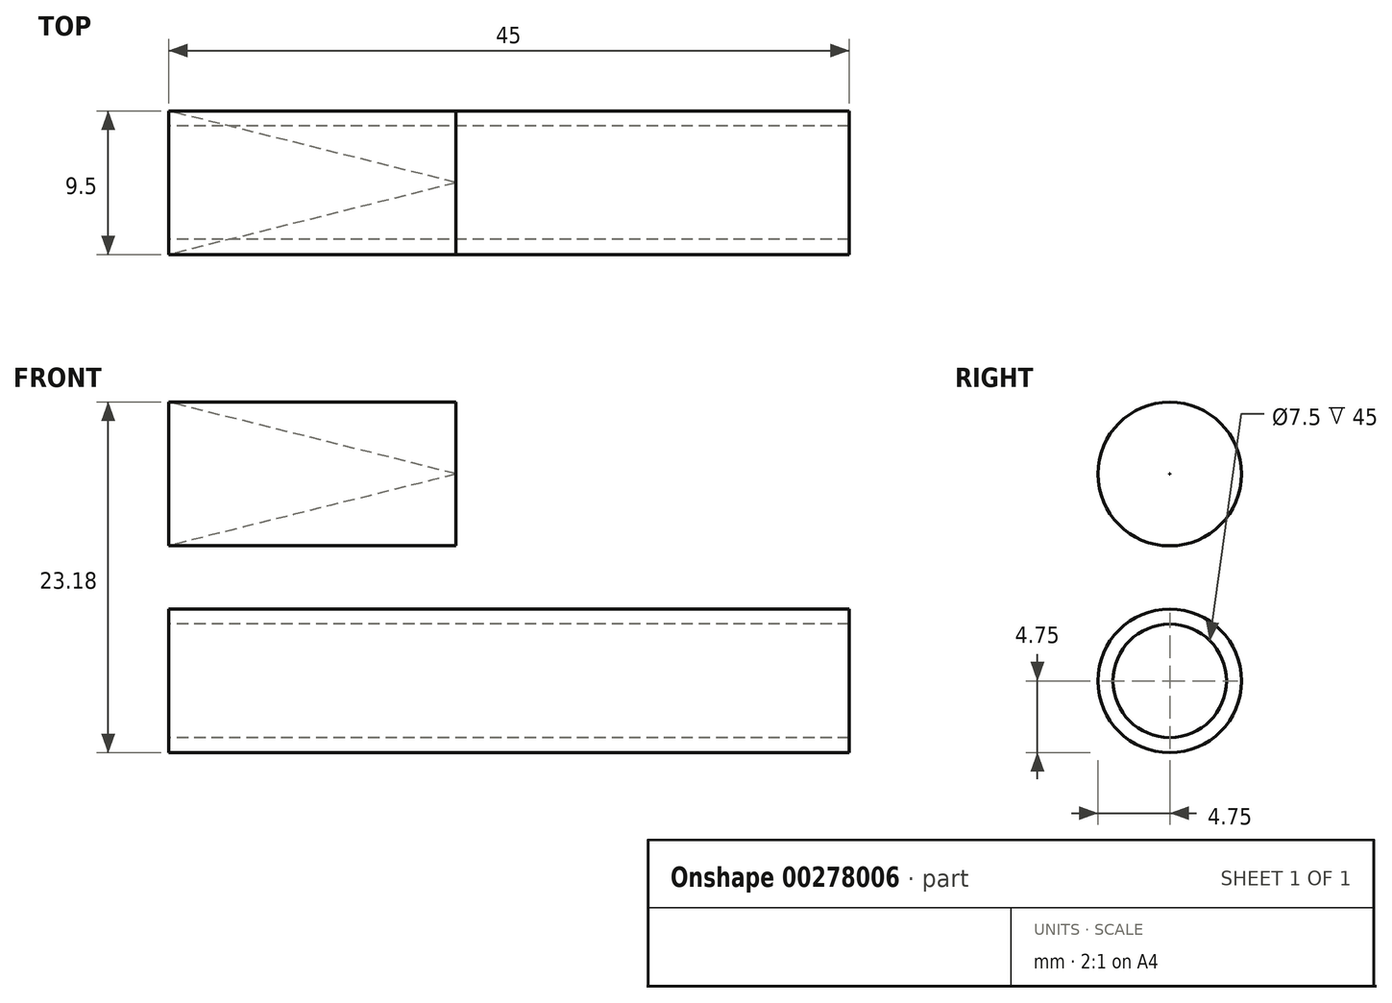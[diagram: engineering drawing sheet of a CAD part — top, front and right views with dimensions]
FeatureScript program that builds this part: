
annotation { "Feature Type Name" : "Feature", "Feature Type Description" : "" }
export const myFeature = defineFeature(function(context is Context, id is Id, definition is map)
    precondition{}
    {
        {
            var Q0;
            Q0=qCreatedBy(makeId("Right.planeOp"),FACE);
            var sketch = newSketch(context, id + "F0", { "sketchPlane" : qUnion([Q0])});
            skCircle(sketch, "E0", {"center": v(0, 0) * mm, "radius": 3.75 * mm});
            skCircle(sketch, "E1", {"center": v(0, 0) * mm, "radius": 4.75 * mm});
            skSolve(sketch);
        }
        {
            var Q0;
            Q0 = qSketchRegion(id + "F0", true);
            extrude(context, id + "F1", {"entities" : qUnion([Q0]), "depth" : 45 * mm});
        }
        {
            var Q0;
            Q0=qCreatedBy(makeId("Right.planeOp"),FACE);
            var sketch = newSketch(context, id + "F2", { "sketchPlane" : qUnion([Q0])});
            skCircle(sketch, "E2", {"center": v(0, 13.68) * mm, "radius": 4.75 * mm});
            skSolve(sketch);
        }
        {
            var Q0;
            Q0 = qSketchRegion(id + "F2", true);
            extrude(context, id + "F3", {"entities" : qUnion([Q0]), "depth" : 19 * mm});
        }
        {
            var Q0;
            Q0=makeQuery(id+"F3.opExtrude","CAP_FACE",FACE,{"disambiguationData":[OSD([sQuery(id+"F2.wireOp",EDGE,"E2")])],"isStart":true});
            extrude(context, id + "F4", {"entities" : qUnion([Q0]), "operationType" : NewBodyOperationType.REMOVE, "oppositeDirection" : true, "depth" : 24.56 * mm, "hasDraft" : true, "draftAngle" : 14 * degree, "draftPullDirection" : true});
        }
    });
